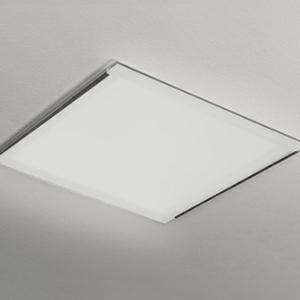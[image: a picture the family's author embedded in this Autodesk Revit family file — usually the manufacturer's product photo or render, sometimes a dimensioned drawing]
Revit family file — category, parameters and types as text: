
# Revit family: 3f_filippi_-_lucequadro_sop_3f_filippi_-_36587_-_lucequadro_led_2000_sop
name_source: partatom
category: Lighting Fixtures
units: mm (PartAtom-declared; Revit-internal decimal feet)

## family parameters
Cut with Voids When Loaded = No
Host = Face
Light Source = No
Part Type = Normal
Room Calculation Point = No
Round Connector Dimension = Use Diameter
Shared = No

## types (1)
- 3F Filippi - Lucequadro SOP (1 x LED, 2238 lm, 20 W, 4000 K)
    Apparent Load = 20 VA
    Approval mark = ENEC
    CIE Flux Codes = 50 81 96 100 100
    Color Rendering = 80
    Color Temperature = 4000 K
    Control Gear = Electronic ballast
    Default Elevation = 1800 mm
    Description = ILLUMINOTECHNICAL
Luminous efficiency 100% (DLOR 100%, ULOR 0%).
Initial luminous flux of the luminaire 2238 lm.
Direct distribution with soft, diffused and controlled light.
Installation Interdistance Transv.D = 1.16 x hu - Long.D = 1.17 x hu.
Tabular UGR (CIE 117 - 4H-8H; S=0.25H; 70/50/20): RUG 24.7 - 24.8.
Beam angle: 101° - 102°.
Luminous efficacy 112 lm/W.
Lifetime (L90/B10): 30000 h. (tq+25°C)
Lifetime (L85/B10): 50000 h. (tq+25°C)
Lifetime (L70/B10): 80000 h. (tq+25°C)
Sudden decreased luminous flux after 50000 hours: 0% (C0).
Photobiological safety in compliance with IEC/TR 62778: RG1 low risk, (IEC 62471).
In compliance with IEC/EN 62722-2-1 - IEC/EN 62717 standards.

SOURCE
Compact LED module 2000/840.
Energy efficiency class (UE 2019/2020 - UE 2019/2015): D.
CIE 13.3 Colour rendering index: CRI >80 (R9 <50%).
IES TM-30 Fidelity Index: Rf = 84 Rg = 95.
CCT nominal colour temperature 4000 K.
Colour initial tolerance (MacAdam): SDCM 3.
Zhaga Book 3 compliant.

MECHANICAL
Housing in white painted steel.
Passive heat dissipator in anodised aluminium, oversized, for optimum thermal management of the LED module.
Flow recuperator in specular aluminium with superficial titanium-magnesium treatment, non-iridescent.
Diffuser in opal methacrylate (PMMA).
Lock-in mounting of the glass in the lateral seats in specular aluminium.
Fixing brackets in galvanised steel.
Slot-cover polycarbonate casings.
Dimensions: 235x235 mm, height 116 mm. Weight 1.815 kg.
IP44 protection degree for exposed part, IP20 for recessed part.
Mechanical strength to impacts IK08 (5 joule).
Glow-wire test resistance 960°C.

ELECTRICAL
Wiring on a separate unit.
Halogen Free electronic wiring 230V-50/60Hz, power factor 0.95, THD <25%, constant output current, SELV, class II, 1 driver.
Power of the luminaire 20 W.
CE - IEC 60598-1 - EN 60598-1.
SAFE FLICKER: PstLM=<1 and SVM=<0.4 (IEC TR 61547-1 and IEC TR 63158), to ensure a more comfortable and safe light.
Ambient temperature from 0°C to +25°C.
Temperature class T6 max 85°C.
Relative humidity UR: <85%.

INSTALLATION
Pull-up recessed fitting.
False ceiling carving: 210x210 mm.
All accessories dedicated to this product are available on the Catalog and on our website www.3F-Filippi.com.

ACCESSORIES
A0189 - Pair of reinforcing brackets for mineral fibre, metal and plasterboard panels, height 20 mm.

APPLICATIONS
Transit areas, corridors, commercial environments, display areas, shops and shop windows.

WARNING
Luminaire designed for disposal/recycling at end-of-life.
Replaceable (LED only) light source by a professional. Replaceable control gear by a professional.
    Height = 0 mm  [stored 0 ft]
    Lamp = 1 x LED
    Lamp Light Flux = 2238 lm
    Lamp Power = 20 W
    Lamp count = 1
    Length = 235 mm
    Lifetime = 50000 h
    Luminous efficacy = 112 lm/W
    Manufacturer = 3F Filippi
    ModVariant = No
    Model = 3F Filippi - 36587 - Lucequadro LED 2000 SOP
    Mounting Place = Ceiling
    Mounting Type = Recessed
    Number of Poles = 1
    OnlyDefault = Yes
    Power Factor = 1
    Product Name = 3F Filippi - Lucequadro SOP
    Product group = recessed luminaire
    ProductGroupID = 4
    Protection Class = Protection class II
    Protection Degree = IP 20
    RLX_Detail_Level = 1
    RLX_Emergency_Light_Flux = 0 lm
    RLX_Emergency_Type = 0
    RLX_Emergency_Type_DB = No
    RlxData = <blob elided: 53993 chars, md5=3ed86927>
    Socket = socket
    Standby Power = 0 W
    System Light Flux = 2238 lm
    System Power = 20 W
    Type Comments = Product without accessories
    Type Image = 3ffilippi_36587.jpg
    URL = http://relux.com
    VarID = ---
    Voltage = 0 V
    Weight = 0.00 kg
    Width = 235 mm

note: [stored X ft] marks values corroborated as IEEE doubles in the binary element streams (Revit-internal decimal feet)

## geometry (parser evidence)
native form markers: Blend x4, Sweep x11
no freeform markers — native parametric forms only
